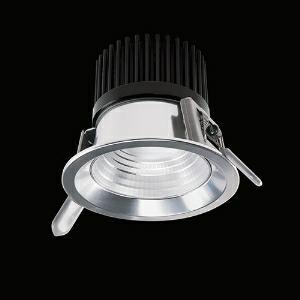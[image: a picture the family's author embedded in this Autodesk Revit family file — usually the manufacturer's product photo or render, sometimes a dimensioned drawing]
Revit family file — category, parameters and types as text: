
# Revit family: spectral_myral_myral_4500-840-f-dali
name_source: partatom
category: Lighting Fixtures
revit_build: Autodesk Revit 2016 (Build: 20150220_1215(x64)
units: mm (PartAtom-declared; Revit-internal decimal feet)

## family parameters
Cut with Voids When Loaded = No
Host = Face
Light Source = No
Part Type = Normal
Room Calculation Point = No
Round Connector Dimension = Use Diameter
Shared = No

## types (1)
- SPECTRAL MYRAL (1 x )
    Apparent Load = 0 VA
    Approval mark = CE
    CIE Flux Codes = 81 99 100 100 100
    Control Gear = Electronic transformer
    Default Elevation = 1800 mm
    Description = SPG0330189
MYRAL recessed spot

Design:
    Height = 0 mm  [stored 0 ft]
    Lamp = 1 x
    Lamp count = 1
    Length = 120 mm
    Luminous efficacy = 0 lm/W
    Manufacturer = Ridi
    ModVariant = No
    Model = MYRAL 4500-840-F-DALI
    Mounting Place = Ceiling
    Mounting Type = Recessed
    Number of Poles = 1
    OnlyDefault = Yes
    Power Factor = 1
    Product Name = SPECTRAL MYRAL
    Product group = Downlight recessed
    ProductGroupID = 400
    Protection Class = Protection class
    Protection Degree = IP 20
    RlxData = <blob elided: 38905 chars, md5=e17e17a7>
    Socket = socket
    Standby Power = 0 W
    System Light Flux = 0 lm
    System Power = 0 W
    Type Image = myral_04.jpg
    URL = http://reluxnet.relux.com
    VarID = ---
    Voltage = 0 V
    Weight = 0.00 kg
    Width = 0 mm  [stored 0 ft]

note: [stored X ft] marks values corroborated as IEEE doubles in the binary element streams (Revit-internal decimal feet)

## geometry (parser evidence)
native form markers: Sweep x11
no freeform markers — native parametric forms only
